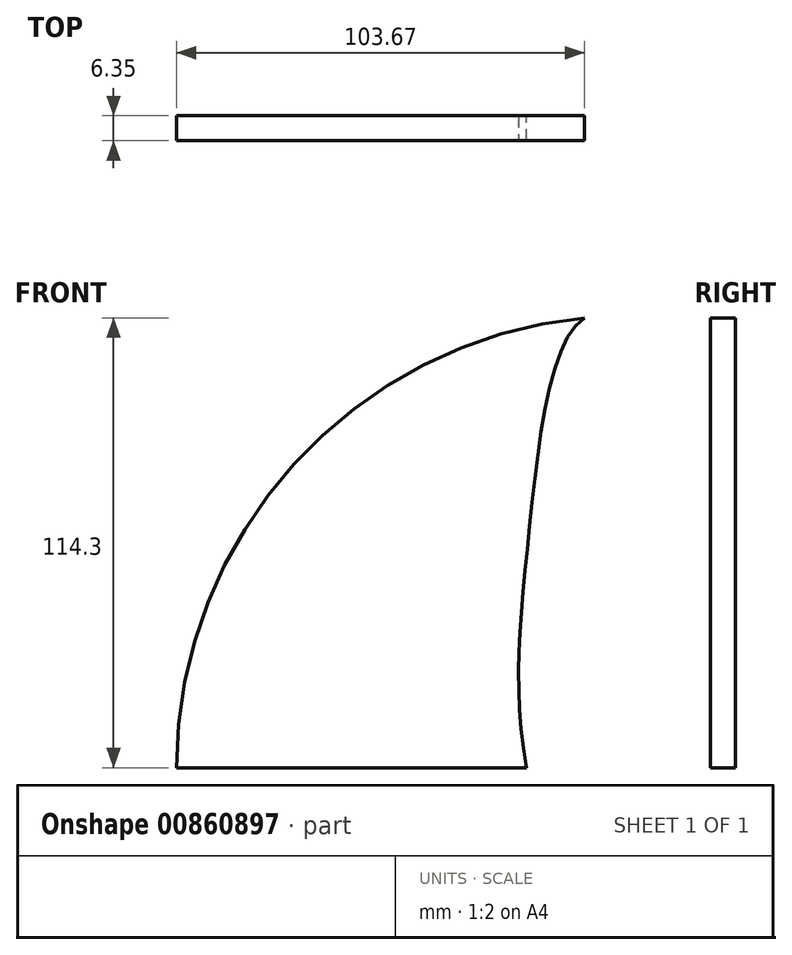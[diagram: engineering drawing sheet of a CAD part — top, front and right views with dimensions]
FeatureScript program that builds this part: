
annotation { "Feature Type Name" : "Feature", "Feature Type Description" : "" }
export const myFeature = defineFeature(function(context is Context, id is Id, definition is map)
    precondition{}
    {
        {
            var Q0;
            Q0=qCreatedBy(makeId("Front.planeOp"),FACE);
            var sketch = newSketch(context, id + "F0", { "sketchPlane" : qUnion([Q0])});
            skLineSegment(sketch, "E0", {"start": v(-38.46, 0) * mm, "end": v(50.44, 0) * mm});
            skArc(sketch, "E1", {"start": v(65.2, 114.3) * mm, "mid": v(-8.64, 77.12) * mm, "end": v(-38.46, 0) * mm});
            skFitSpline(sketch, "E2", {"points": [v(65.2, 114.3) * mm, v(51, 59.11) * mm, v(50.44, 0) * mm], "startDerivative": vector(-56.26, -35.48) * mm, "endDerivative": vector(21.3, -115.79) * mm});
            skSolve(sketch);
        }
        {
            var Q0;
            Q0 = qSketchRegion(id + "F0", true);
            extrude(context, id + "F1", {"entities" : qUnion([Q0]), "depth" : 6.35 * mm, "offsetDistance" : 25.4 * mm});
        }
    });
